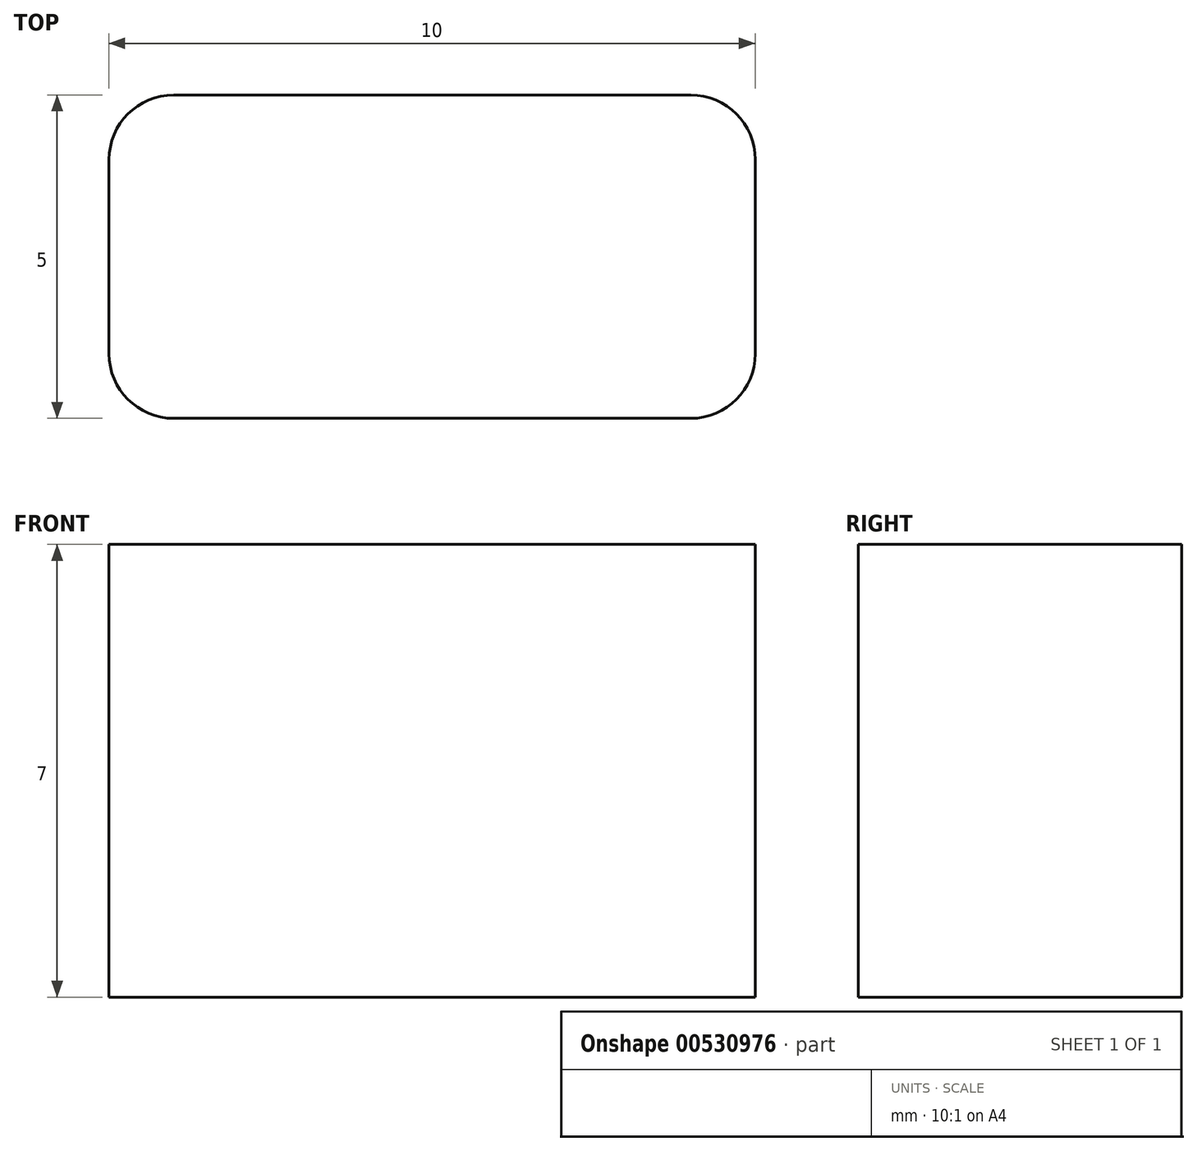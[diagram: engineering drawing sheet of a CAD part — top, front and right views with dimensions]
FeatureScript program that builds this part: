
annotation { "Feature Type Name" : "Feature", "Feature Type Description" : "" }
export const myFeature = defineFeature(function(context is Context, id is Id, definition is map)
    precondition{}
    {
        {
            var Q0;
            Q0=qCreatedBy(makeId("Top.planeOp"),FACE);
            var sketch = newSketch(context, id + "F0", { "sketchPlane" : qUnion([Q0])});
            skLineSegment(sketch, "E0.bottom", {"start": v(-13.54, -2.6) * mm, "end": v(-5.54, -2.6) * mm});
            skLineSegment(sketch, "E0.top", {"start": v(-13.54, -7.6) * mm, "end": v(-5.54, -7.6) * mm});
            skLineSegment(sketch, "E0.left", {"start": v(-14.54, -3.6) * mm, "end": v(-14.54, -6.6) * mm});
            skLineSegment(sketch, "E0.right", {"start": v(-4.54, -3.6) * mm, "end": v(-4.54, -6.6) * mm});
            skPoint(sketch, "E1.visualSharp", {"position": v(-14.54, -2.6) * mm});
            skArc(sketch, "E1.filletArc", {"start": v(-13.54, -2.6) * mm, "mid": v(-14.24, -2.88) * mm, "end": v(-14.54, -3.6) * mm});
            skPoint(sketch, "E2.visualSharp", {"position": v(-14.54, -7.6) * mm});
            skArc(sketch, "E2.filletArc", {"start": v(-14.54, -6.6) * mm, "mid": v(-14.24, -7.3) * mm, "end": v(-13.54, -7.6) * mm});
            skPoint(sketch, "E3.visualSharp", {"position": v(-4.54, -2.6) * mm});
            skArc(sketch, "E3.filletArc", {"start": v(-4.54, -3.6) * mm, "mid": v(-4.83, -2.88) * mm, "end": v(-5.54, -2.6) * mm});
            skPoint(sketch, "E4.visualSharp", {"position": v(-4.54, -7.6) * mm});
            skArc(sketch, "E4.filletArc", {"start": v(-5.54, -7.6) * mm, "mid": v(-4.83, -7.3) * mm, "end": v(-4.54, -6.6) * mm});
            skSolve(sketch);
        }
        {
            var Q0;
            Q0=makeQuery(id+"F0.imprint","IMPRINT",FACE,{"disambiguationData":[TD([[makeQuery(id+"F0.imprint","IMPRINT",EDGE,{"derivedFrom":sQuery(id+"F0.wireOp",EDGE,"E0.bottom")}),-1.0]])]});
            extrude(context, id + "F1", {"entities" : qUnion([Q0]), "depth" : 7 * mm, "offsetDistance" : 25 * mm});
        }
    });
